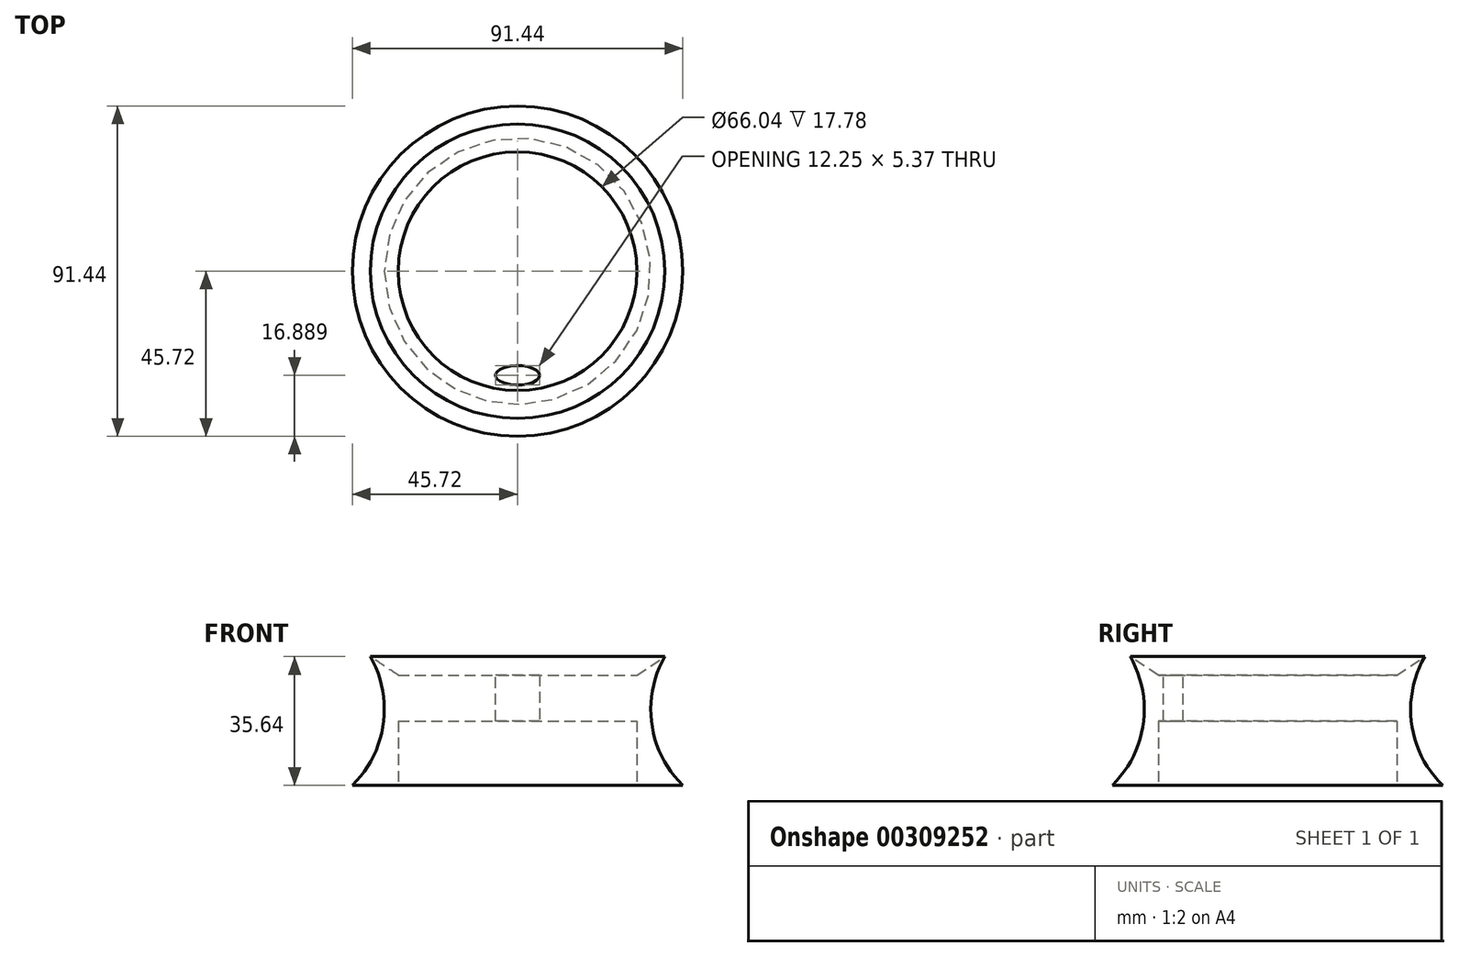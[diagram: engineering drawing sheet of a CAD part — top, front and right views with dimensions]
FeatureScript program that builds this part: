
annotation { "Feature Type Name" : "Feature", "Feature Type Description" : "" }
export const myFeature = defineFeature(function(context is Context, id is Id, definition is map)
    precondition{}
    {
        {
            var Q0;
            Q0=qCreatedBy(makeId("Front.planeOp"),FACE);
            var sketch = newSketch(context, id + "F0", { "sketchPlane" : qUnion([Q0])});
            skLineSegment(sketch, "E0", {"start": v(33.02, 19.68) * mm, "end": v(40.76, 24.84) * mm});
            skLineSegment(sketch, "E1", {"start": v(45.72, -10.8) * mm, "end": v(33.02, -10.8) * mm});
            skLineSegment(sketch, "E2", {"start": v(33.02, -10.8) * mm, "end": v(33.02, 6.98) * mm});
            skLineSegment(sketch, "E3", {"start": v(0, 6.98) * mm, "end": v(0, 19.68) * mm});
            skLineSegment(sketch, "E4", {"start": v(33.02, 19.68) * mm, "end": v(0, 19.68) * mm});
            skLineSegment(sketch, "E5", {"start": v(0, 6.98) * mm, "end": v(33.02, 6.98) * mm});
            skArc(sketch, "E6", {"start": v(40.76, 24.84) * mm, "mid": v(37.16, 6.17) * mm, "end": v(45.72, -10.8) * mm});
            skSolve(sketch);
        }
        {
            var Q0;
            Q0=makeQuery(id+"F0.imprint","IMPRINT",FACE,{"disambiguationData":[TD([[makeQuery(id+"F0.imprint","IMPRINT",EDGE,{"derivedFrom":sQuery(id+"F0.wireOp",EDGE,"E0")}),-1.0]])]});
            var Q1;
            Q1=sQuery(id+"F0.wireOp",EDGE,"E3");
            revolve(context, id + "F1", {"entities" : qUnion([Q0]), "axis" : qUnion([Q1]), "revolveType" : RevolveType.FULL});
        }
        {
            var Q0;
            Q0=qCreatedBy(makeId("Top.planeOp"),FACE);
            var sketch = newSketch(context, id + "F2", { "sketchPlane" : qUnion([Q0])});
            skEllipse(sketch, "E7", {"center": v(0, -28.83) * mm, "majorRadius": 6.13 * mm, "minorRadius": 2.69 * mm, "majorAxis": v(1, 0)});
            skSolve(sketch);
        }
        {
            var Q0;
            Q0 = qSketchRegion(id + "F2", true);
            extrude(context, id + "F3", {"entities" : qUnion([Q0]), "operationType" : NewBodyOperationType.REMOVE, "endBound" : BoundingType.SYMMETRIC, "depth" : 50.8 * mm});
        }
    });
